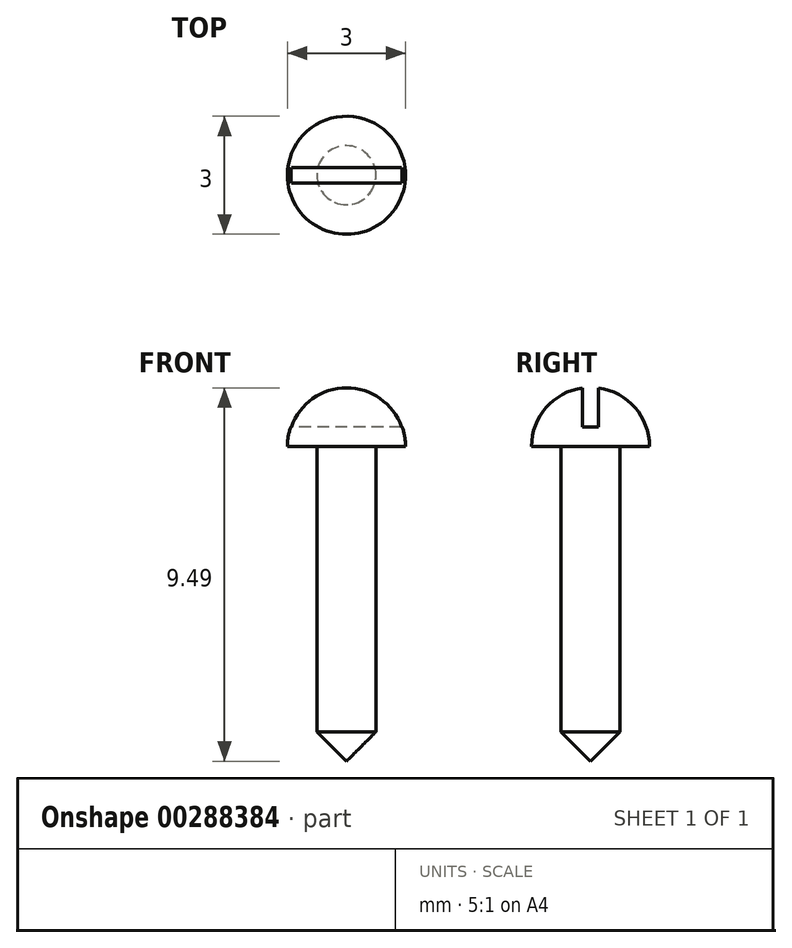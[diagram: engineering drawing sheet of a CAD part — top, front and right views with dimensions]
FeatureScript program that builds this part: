
annotation { "Feature Type Name" : "Feature", "Feature Type Description" : "" }
export const myFeature = defineFeature(function(context is Context, id is Id, definition is map)
    precondition{}
    {
        {
            var Q0;
            Q0=qCreatedBy(makeId("Front.planeOp"),FACE);
            var sketch = newSketch(context, id + "F0", { "sketchPlane" : qUnion([Q0])});
            skLineSegment(sketch, "E0", {"start": v(0, 0) * mm, "end": v(0, 9.5) * mm});
            skLineSegment(sketch, "E1", {"start": v(0.75, 8) * mm, "end": v(1.5, 8) * mm});
            skLineSegment(sketch, "E2.1", {"start": v(0.75, 0.75) * mm, "end": v(0.75, 8) * mm});
            skLineSegment(sketch, "E3", {"start": v(0, 0) * mm, "end": v(0.75, 0.75) * mm});
            skArc(sketch, "E4.trimOffspring", {"start": v(1.5, 8) * mm, "mid": v(1.06, 9.06) * mm, "end": v(0, 9.5) * mm});
            skSolve(sketch);
        }
        {
            var Q0;
            Q0 = qSketchRegion(id + "F0", true);
            var Q1;
            Q1=sQuery(id+"F0.wireOp",EDGE,"E0");
            revolve(context, id + "F1", {"entities" : qUnion([Q0]), "axis" : qUnion([Q1]), "revolveType" : RevolveType.FULL});
        }
        {
            var Q0;
            Q0=qCreatedBy(makeId("Top.planeOp"),FACE);
            cPlane(context, id + "F2", {"entities" : qUnion([Q0]), "cplaneType" : CPlaneType.OFFSET, "offset" : 9.5 * mm, "width" : 150 * mm, "height" : 150 * mm});
        }
        {
            var Q0;
            Q0=qCreatedBy(id+"F2.planeOp",FACE);
            var sketch = newSketch(context, id + "F3", { "sketchPlane" : qUnion([Q0])});
            skLineSegment(sketch, "E5.bottom", {"start": v(1.5, -0.2) * mm, "end": v(-1.5, -0.2) * mm});
            skLineSegment(sketch, "E5.top", {"start": v(1.5, 0.2) * mm, "end": v(-1.5, 0.2) * mm});
            skLineSegment(sketch, "E5.left", {"start": v(1.5, -0.2) * mm, "end": v(1.5, 0.2) * mm});
            skLineSegment(sketch, "E5.right", {"start": v(-1.5, -0.2) * mm, "end": v(-1.5, 0.2) * mm});
            skPoint(sketch, "E5.middle", {"position": v(0, 0) * mm});
            skSolve(sketch);
        }
        {
            var Q0;
            Q0=makeQuery(id+"F3.imprint","IMPRINT",FACE,{"disambiguationData":[TD([[makeQuery(id+"F3.imprint","IMPRINT",EDGE,{"derivedFrom":sQuery(id+"F3.wireOp",EDGE,"E5.bottom")}),-1.0]])]});
            extrude(context, id + "F4", {"entities" : qUnion([Q0]), "operationType" : NewBodyOperationType.REMOVE, "oppositeDirection" : true, "depth" : 1 * mm});
        }
    });
